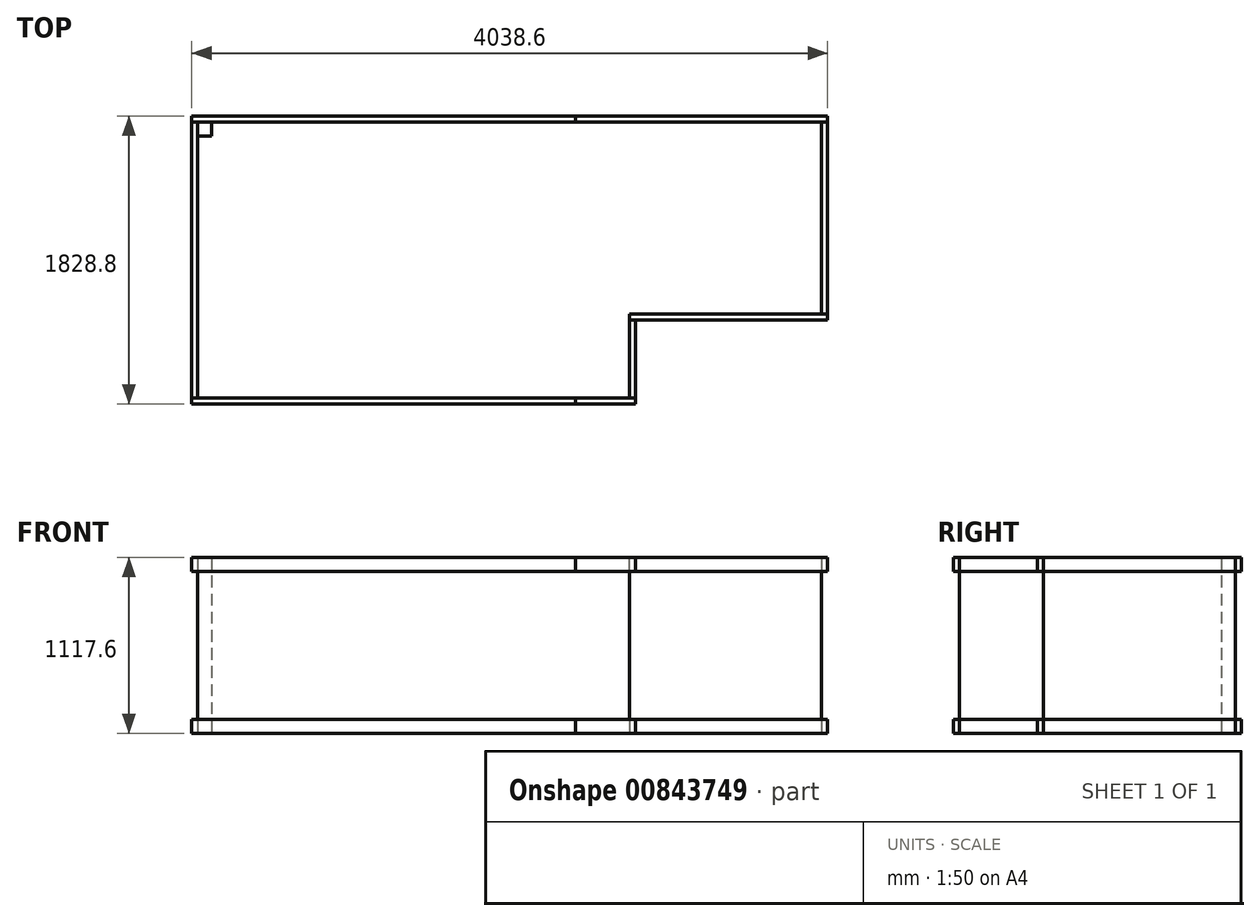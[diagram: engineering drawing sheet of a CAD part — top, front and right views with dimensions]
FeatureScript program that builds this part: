
annotation { "Feature Type Name" : "Feature", "Feature Type Description" : "" }
export const myFeature = defineFeature(function(context is Context, id is Id, definition is map)
    precondition{}
    {
        {
            var Q0;
            Q0=qCreatedBy(makeId("Top.planeOp"),FACE);
            var sketch = newSketch(context, id + "F0", { "sketchPlane" : qUnion([Q0])});
            skLineSegment(sketch, "E0", {"start": v(0, 0) * mm, "end": v(0, -1752.6) * mm});
            skLineSegment(sketch, "E1", {"start": v(0, -1752.6) * mm, "end": v(2743.2, -1752.6) * mm});
            skLineSegment(sketch, "E2", {"start": v(2743.2, -1752.6) * mm, "end": v(2743.2, -1219.2) * mm});
            skLineSegment(sketch, "E3", {"start": v(2743.2, -1219.2) * mm, "end": v(3962.4, -1219.2) * mm});
            skLineSegment(sketch, "E4", {"start": v(3962.4, -1219.2) * mm, "end": v(3962.4, 0) * mm});
            skLineSegment(sketch, "E5", {"start": v(3962.4, 0) * mm, "end": v(0, 0) * mm});
            skSolve(sketch);
        }
        {
            var Q0;
            Q0 = qSketchRegion(id + "F0", true);
            extrude(context, id + "F1", {"entities" : qUnion([Q0]), "depth" : 1117.6 * mm, "offsetDistance" : 25.4 * mm});
        }
        {
            var Q0;
            Q0=qCreatedBy(makeId("Top.planeOp"),FACE);
            var sketch = newSketch(context, id + "F2", { "sketchPlane" : qUnion([Q0])});
            skLineSegment(sketch, "E6.bottom", {"start": v(-38.1, -1752.6) * mm, "end": v(2400.3, -1752.6) * mm});
            skLineSegment(sketch, "E6.top", {"start": v(-38.1, -1790.7) * mm, "end": v(2400.3, -1790.7) * mm});
            skLineSegment(sketch, "E6.left", {"start": v(-38.1, -1752.6) * mm, "end": v(-38.1, -1790.7) * mm});
            skLineSegment(sketch, "E6.right", {"start": v(2400.3, -1752.6) * mm, "end": v(2400.3, -1790.7) * mm});
            skSolve(sketch);
        }
        {
            var Q0;
            Q0 = qSketchRegion(id + "F2", true);
            extrude(context, id + "F3", {"entities" : qUnion([Q0]), "depth" : 88.9 * mm, "offsetDistance" : 25.4 * mm});
        }
        {
            var Q0;
            Q0=qCreatedBy(makeId("Top.planeOp"),FACE);
            var sketch = newSketch(context, id + "F4", { "sketchPlane" : qUnion([Q0])});
            skLineSegment(sketch, "E7.bottom", {"start": v(-38.1, 0) * mm, "end": v(2400.3, 0) * mm});
            skLineSegment(sketch, "E7.top", {"start": v(-38.1, 38.1) * mm, "end": v(2400.3, 38.1) * mm});
            skLineSegment(sketch, "E7.left", {"start": v(-38.1, 0) * mm, "end": v(-38.1, 38.1) * mm});
            skLineSegment(sketch, "E7.right", {"start": v(2400.3, 0) * mm, "end": v(2400.3, 38.1) * mm});
            skSolve(sketch);
        }
        {
            var Q0;
            Q0 = qSketchRegion(id + "F4", true);
            extrude(context, id + "F5", {"entities" : qUnion([Q0]), "depth" : 88.9 * mm, "offsetDistance" : 25.4 * mm});
        }
        {
            var Q0;
            Q0=qCreatedBy(makeId("Top.planeOp"),FACE);
            var sketch = newSketch(context, id + "F6", { "sketchPlane" : qUnion([Q0])});
            skLineSegment(sketch, "E8.bottom", {"start": v(-38.1, 0) * mm, "end": v(0, 0) * mm});
            skLineSegment(sketch, "E8.top", {"start": v(-38.1, -1752.6) * mm, "end": v(0, -1752.6) * mm});
            skLineSegment(sketch, "E8.left", {"start": v(-38.1, 0) * mm, "end": v(-38.1, -1752.6) * mm});
            skLineSegment(sketch, "E8.right", {"start": v(0, 0) * mm, "end": v(0, -1752.6) * mm});
            skSolve(sketch);
        }
        {
            var Q0;
            Q0 = qSketchRegion(id + "F6", true);
            extrude(context, id + "F7", {"entities" : qUnion([Q0]), "depth" : 88.9 * mm, "offsetDistance" : 25.4 * mm});
        }
        {
            var Q0;
            Q0=qCreatedBy(makeId("Top.planeOp"),FACE);
            var sketch = newSketch(context, id + "F8", { "sketchPlane" : qUnion([Q0])});
            skLineSegment(sketch, "E9.bottom", {"start": v(2400.3, 38.1) * mm, "end": v(4000.5, 38.1) * mm});
            skLineSegment(sketch, "E9.top", {"start": v(2400.3, 0) * mm, "end": v(4000.5, 0) * mm});
            skLineSegment(sketch, "E9.left", {"start": v(2400.3, 38.1) * mm, "end": v(2400.3, 0) * mm});
            skLineSegment(sketch, "E9.right", {"start": v(4000.5, 38.1) * mm, "end": v(4000.5, 0) * mm});
            skSolve(sketch);
        }
        {
            var Q0;
            Q0 = qSketchRegion(id + "F8", true);
            extrude(context, id + "F9", {"entities" : qUnion([Q0]), "depth" : 88.9 * mm, "offsetDistance" : 25.4 * mm});
        }
        {
            var Q0;
            Q0=qCreatedBy(makeId("Top.planeOp"),FACE);
            var sketch = newSketch(context, id + "F10", { "sketchPlane" : qUnion([Q0])});
            skLineSegment(sketch, "E10.bottom", {"start": v(2400.3, -1790.7) * mm, "end": v(2781.3, -1790.7) * mm});
            skLineSegment(sketch, "E10.top", {"start": v(2400.3, -1752.6) * mm, "end": v(2781.3, -1752.6) * mm});
            skLineSegment(sketch, "E10.left", {"start": v(2400.3, -1790.7) * mm, "end": v(2400.3, -1752.6) * mm});
            skLineSegment(sketch, "E10.right", {"start": v(2781.3, -1790.7) * mm, "end": v(2781.3, -1752.6) * mm});
            skSolve(sketch);
        }
        {
            var Q0;
            Q0 = qSketchRegion(id + "F10", true);
            extrude(context, id + "F11", {"entities" : qUnion([Q0]), "depth" : 88.9 * mm, "offsetDistance" : 25.4 * mm});
        }
        {
            var Q0;
            Q0=qCreatedBy(makeId("Top.planeOp"),FACE);
            var sketch = newSketch(context, id + "F12", { "sketchPlane" : qUnion([Q0])});
            skLineSegment(sketch, "E11.bottom", {"start": v(2743.2, -1257.3) * mm, "end": v(4000.5, -1257.3) * mm});
            skLineSegment(sketch, "E11.top", {"start": v(2743.2, -1219.2) * mm, "end": v(4000.5, -1219.2) * mm});
            skLineSegment(sketch, "E11.left", {"start": v(2743.2, -1257.3) * mm, "end": v(2743.2, -1219.2) * mm});
            skLineSegment(sketch, "E11.right", {"start": v(4000.5, -1257.3) * mm, "end": v(4000.5, -1219.2) * mm});
            skSolve(sketch);
        }
        {
            var Q0;
            Q0 = qSketchRegion(id + "F12", true);
            extrude(context, id + "F13", {"entities" : qUnion([Q0]), "depth" : 88.9 * mm, "offsetDistance" : 25.4 * mm});
        }
        {
            var Q0;
            Q0=qCreatedBy(makeId("Top.planeOp"),FACE);
            var sketch = newSketch(context, id + "F14", { "sketchPlane" : qUnion([Q0])});
            skLineSegment(sketch, "E12.bottom", {"start": v(2781.3, -1752.6) * mm, "end": v(2743.2, -1752.6) * mm});
            skLineSegment(sketch, "E12.top", {"start": v(2781.3, -1257.3) * mm, "end": v(2743.2, -1257.3) * mm});
            skLineSegment(sketch, "E12.left", {"start": v(2781.3, -1752.6) * mm, "end": v(2781.3, -1257.3) * mm});
            skLineSegment(sketch, "E12.right", {"start": v(2743.2, -1752.6) * mm, "end": v(2743.2, -1257.3) * mm});
            skSolve(sketch);
        }
        {
            var Q0;
            Q0 = qSketchRegion(id + "F14", true);
            extrude(context, id + "F15", {"entities" : qUnion([Q0]), "depth" : 88.9 * mm, "offsetDistance" : 25.4 * mm});
        }
        {
            var Q0;
            Q0=qCreatedBy(makeId("Top.planeOp"),FACE);
            var sketch = newSketch(context, id + "F16", { "sketchPlane" : qUnion([Q0])});
            skLineSegment(sketch, "E13.bottom", {"start": v(3962.4, 0) * mm, "end": v(4000.5, 0) * mm});
            skLineSegment(sketch, "E13.top", {"start": v(3962.4, -1219.2) * mm, "end": v(4000.5, -1219.2) * mm});
            skLineSegment(sketch, "E13.left", {"start": v(3962.4, 0) * mm, "end": v(3962.4, -1219.2) * mm});
            skLineSegment(sketch, "E13.right", {"start": v(4000.5, 0) * mm, "end": v(4000.5, -1219.2) * mm});
            skSolve(sketch);
        }
        {
            var Q0;
            Q0 = qSketchRegion(id + "F16", true);
            extrude(context, id + "F17", {"entities" : qUnion([Q0]), "depth" : 88.9 * mm, "offsetDistance" : 25.4 * mm});
        }
        {
            var Q0;
            Q0=qCreatedBy(makeId("Top.planeOp"),FACE);
            cPlane(context, id + "F18", {"entities" : qUnion([Q0]), "cplaneType" : CPlaneType.OFFSET, "offset" : 558.8 * mm, "width" : 152.4 * mm, "height" : 152.4 * mm});
        }
        {
            var Q0;
            Q0=makeQuery(id+"F3.opExtrude","SWEPT_BODY",BODY,{"disambiguationData":[OSD([sQuery(id+"F2.wireOp",EDGE,"E6.bottom"),sQuery(id+"F2.wireOp",EDGE,"E6.top"),sQuery(id+"F2.wireOp",EDGE,"E6.left"),sQuery(id+"F2.wireOp",EDGE,"E6.right")])]});
            var Q1;
            Q1=makeQuery(id+"F5.opExtrude","SWEPT_BODY",BODY,{"disambiguationData":[OSD([sQuery(id+"F4.wireOp",EDGE,"E7.bottom"),sQuery(id+"F4.wireOp",EDGE,"E7.top"),sQuery(id+"F4.wireOp",EDGE,"E7.left"),sQuery(id+"F4.wireOp",EDGE,"E7.right")])]});
            var Q2;
            Q2=makeQuery(id+"F7.opExtrude","SWEPT_BODY",BODY,{"disambiguationData":[OSD([sQuery(id+"F6.wireOp",EDGE,"E8.bottom"),sQuery(id+"F6.wireOp",EDGE,"E8.top"),sQuery(id+"F6.wireOp",EDGE,"E8.left"),sQuery(id+"F6.wireOp",EDGE,"E8.right")])]});
            var Q3;
            Q3=makeQuery(id+"F9.opExtrude","SWEPT_BODY",BODY,{"disambiguationData":[OSD([sQuery(id+"F8.wireOp",EDGE,"E9.bottom"),sQuery(id+"F8.wireOp",EDGE,"E9.top"),sQuery(id+"F8.wireOp",EDGE,"E9.left"),sQuery(id+"F8.wireOp",EDGE,"E9.right")])]});
            var Q4;
            Q4=makeQuery(id+"F11.opExtrude","SWEPT_BODY",BODY,{"disambiguationData":[OSD([sQuery(id+"F10.wireOp",EDGE,"E10.bottom"),sQuery(id+"F10.wireOp",EDGE,"E10.top"),sQuery(id+"F10.wireOp",EDGE,"E10.left"),sQuery(id+"F10.wireOp",EDGE,"E10.right")])]});
            var Q5;
            Q5=makeQuery(id+"F13.opExtrude","SWEPT_BODY",BODY,{"disambiguationData":[OSD([sQuery(id+"F12.wireOp",EDGE,"E11.bottom"),sQuery(id+"F12.wireOp",EDGE,"E11.top"),sQuery(id+"F12.wireOp",EDGE,"E11.left"),sQuery(id+"F12.wireOp",EDGE,"E11.right")])]});
            var Q6;
            Q6=makeQuery(id+"F15.opExtrude","SWEPT_BODY",BODY,{"disambiguationData":[OSD([sQuery(id+"F14.wireOp",EDGE,"E12.bottom"),sQuery(id+"F14.wireOp",EDGE,"E12.top"),sQuery(id+"F14.wireOp",EDGE,"E12.left"),sQuery(id+"F14.wireOp",EDGE,"E12.right")])]});
            var Q7;
            Q7=makeQuery(id+"F17.opExtrude","SWEPT_BODY",BODY,{"disambiguationData":[OSD([sQuery(id+"F16.wireOp",EDGE,"E13.bottom"),sQuery(id+"F16.wireOp",EDGE,"E13.top"),sQuery(id+"F16.wireOp",EDGE,"E13.left"),sQuery(id+"F16.wireOp",EDGE,"E13.right")])]});
            var Q8;
            Q8=qCreatedBy(id+"F18.planeOp",FACE);
            mirror(context, id + "F19", {"entities" : qUnion([Q0, Q1, Q2, Q3, Q4, Q5, Q6, Q7]), "mirrorPlane" : qUnion([Q8])});
        }
        {
            var Q0;
            Q0=makeQuery(id+"F19.opPattern","COPY",BODY,{"derivedFrom":makeQuery(id+"F7.opExtrude","SWEPT_BODY",BODY,{"disambiguationData":[OSD([sQuery(id+"F6.wireOp",EDGE,"E8.bottom"),sQuery(id+"F6.wireOp",EDGE,"E8.top"),sQuery(id+"F6.wireOp",EDGE,"E8.left"),sQuery(id+"F6.wireOp",EDGE,"E8.right")])]}),"instanceName":"1"});
            deleteBodies(context, id + "F20", {"entities" : qUnion([Q0])});
        }
        {
            var Q0;
            Q0=qCreatedBy(makeId("Top.planeOp"),FACE);
            var sketch = newSketch(context, id + "F21", { "sketchPlane" : qUnion([Q0])});
            skLineSegment(sketch, "E14.bottom", {"start": v(0, 0) * mm, "end": v(88.9, 0) * mm});
            skLineSegment(sketch, "E14.top", {"start": v(0, -88.9) * mm, "end": v(88.9, -88.9) * mm});
            skLineSegment(sketch, "E14.left", {"start": v(0, 0) * mm, "end": v(0, -88.9) * mm});
            skLineSegment(sketch, "E14.right", {"start": v(88.9, 0) * mm, "end": v(88.9, -88.9) * mm});
            skSolve(sketch);
        }
        {
            var Q0;
            Q0 = qSketchRegion(id + "F21", true);
            extrude(context, id + "F22", {"entities" : qUnion([Q0]), "depth" : 1117.6 * mm, "offsetDistance" : 25.4 * mm});
        }
    });
